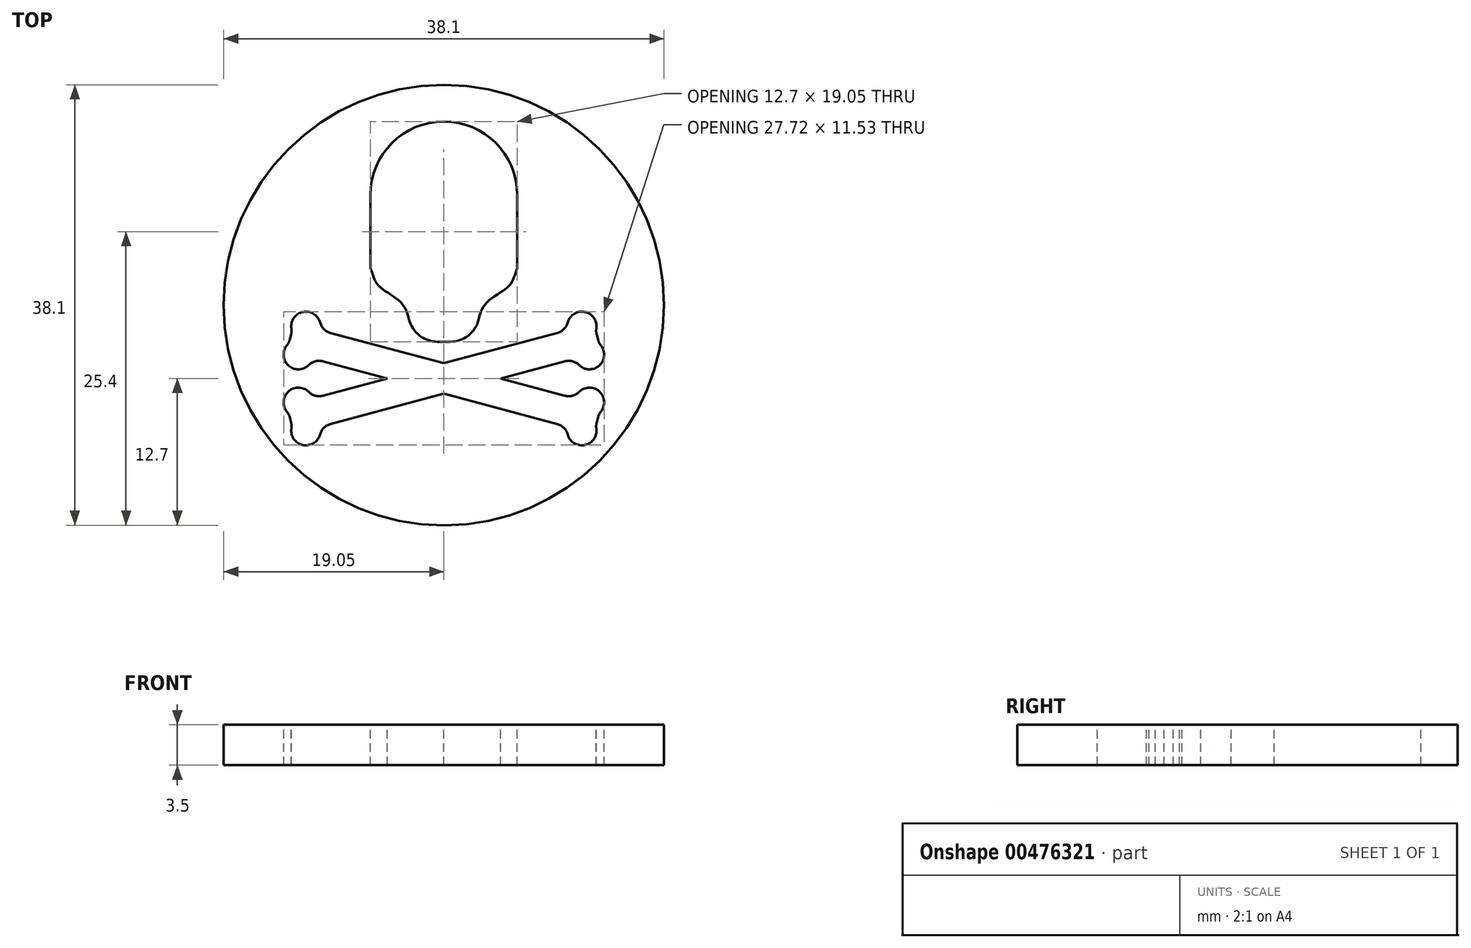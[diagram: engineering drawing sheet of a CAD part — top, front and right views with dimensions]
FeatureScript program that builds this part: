
annotation { "Feature Type Name" : "Feature", "Feature Type Description" : "" }
export const myFeature = defineFeature(function(context is Context, id is Id, definition is map)
    precondition{}
    {
        {
            var Q0;
            Q0=qCreatedBy(makeId("Top.planeOp"),FACE);
            var sketch = newSketch(context, id + "F0", { "sketchPlane" : qUnion([Q0])});
            skCircle(sketch, "E0", {"center": v(0, 0) * mm, "radius": 19.05 * mm});
            skSolve(sketch);
        }
        {
            var Q0;
            Q0=qSketchRegion(id+"F0",true);
            extrude(context, id + "F1", {"entities" : qUnion([Q0]), "depth" : 3.5 * mm});
        }
        {
            var Q0;
            Q0=makeQuery(id+"F1.opExtrude","CAP_FACE",FACE,{"disambiguationData":[OSD([sQuery(id+"F0.wireOp",EDGE,"E0")])],"isStart":false});
            var sketch = newSketch(context, id + "F2", { "sketchPlane" : qUnion([Q0])});
            skLineSegment(sketch, "E1.bottom", {"start": v(0, 15.88) * mm, "end": v(0, 15.88) * mm});
            skLineSegment(sketch, "E1.top", {"start": v(0.54, -3.18) * mm, "end": v(-0.54, -3.18) * mm});
            skLineSegment(sketch, "E1.left", {"start": v(6.35, 9.52) * mm, "end": v(6.35, 3.18) * mm});
            skLineSegment(sketch, "E1.right", {"start": v(-6.35, 9.52) * mm, "end": v(-6.35, 3.17) * mm});
            skPoint(sketch, "E1.middle", {"position": v(0, 6.35) * mm});
            skPoint(sketch, "E2.visualSharp", {"position": v(-6.35, 15.88) * mm});
            skArc(sketch, "E2.filletArc", {"start": v(0, 15.88) * mm, "mid": v(-4.5, 14.02) * mm, "end": v(-6.35, 9.52) * mm});
            skPoint(sketch, "E3.visualSharp", {"position": v(6.35, 15.88) * mm});
            skArc(sketch, "E3.filletArc", {"start": v(6.35, 9.52) * mm, "mid": v(4.5, 14.02) * mm, "end": v(0, 15.88) * mm});
            skFitSpline(sketch, "E4", {"points": [v(-6.35, 3.17) * mm, v(-5.66, 1.69) * mm, v(-3.53, 0) * mm, v(-2.54, -3.18) * mm], "startDerivative": vector(2.39, -5.8) * mm, "endDerivative": vector(3.14, -8.85) * mm});
            skLineSegment(sketch, "E5", {"start": v(0, 15.88) * mm, "end": v(0, -3.18) * mm});
            skFitSpline(sketch, "E6.MirrorCS", {"points": [v(6.35, 3.17) * mm, v(5.66, 1.69) * mm, v(3.53, 0) * mm, v(2.54, -3.17) * mm], "startDerivative": vector(-2.39, -5.8) * mm, "endDerivative": vector(-3.14, -8.85) * mm});
            skPoint(sketch, "E7.orphan", {"position": v(-6.35, -3.17) * mm});
            skPoint(sketch, "E8.orphan", {"position": v(6.35, -3.18) * mm});
            skArc(sketch, "E9.filletArc", {"start": v(-3.01, -1.24) * mm, "mid": v(-2.11, -2.63) * mm, "end": v(-0.54, -3.17) * mm});
            skPoint(sketch, "E10.visualSharp", {"position": v(2.54, -3.18) * mm});
            skArc(sketch, "E10.filletArc", {"start": v(0.54, -3.17) * mm, "mid": v(2.11, -2.63) * mm, "end": v(3.01, -1.24) * mm});
            skSolve(sketch);
        }
        {
            var Q0;
            Q0=qSketchRegion(id+"F2",true);
            extrude(context, id + "F3", {"entities" : qUnion([Q0]), "operationType" : NewBodyOperationType.REMOVE, "oppositeDirection" : true, "depth" : 5.33 * mm});
        }
        {
            var Q0;
            Q0=makeQuery(id+"F1.opExtrude","CAP_FACE",FACE,{"disambiguationData":[OSD([sQuery(id+"F0.wireOp",EDGE,"E0")])],"isStart":false});
            var sketch = newSketch(context, id + "F4", { "sketchPlane" : qUnion([Q0])});
            skLineSegment(sketch, "E11", {"start": v(-11.94, -1.84) * mm, "end": v(12.6, -8.41) * mm});
            skLineSegment(sketch, "E12", {"start": v(12.6, -8.41) * mm, "end": v(11.94, -10.86) * mm});
            skLineSegment(sketch, "E13", {"start": v(11.94, -10.86) * mm, "end": v(-12.6, -4.29) * mm});
            skLineSegment(sketch, "E14", {"start": v(-12.6, -4.29) * mm, "end": v(-11.94, -1.84) * mm});
            skLineSegment(sketch, "E15", {"start": v(-12.27, -3.06) * mm, "end": v(12.27, -9.64) * mm});
            skPoint(sketch, "E16", {"position": v(0, -6.35) * mm});
            skLineSegment(sketch, "E17", {"start": v(-12.6, -8.41) * mm, "end": v(9.81, -2.4) * mm});
            skLineSegment(sketch, "E18", {"start": v(11.94, -1.84) * mm, "end": v(12.6, -4.29) * mm});
            skLineSegment(sketch, "E19", {"start": v(10.47, -4.86) * mm, "end": v(-11.94, -10.86) * mm});
            skLineSegment(sketch, "E20", {"start": v(-11.94, -10.86) * mm, "end": v(-12.6, -8.41) * mm});
            skLineSegment(sketch, "E21", {"start": v(-12.27, -9.64) * mm, "end": v(12.27, -3.06) * mm});
            skLineSegment(sketch, "E22", {"start": v(0, 0) * mm, "end": v(0, -6.35) * mm});
            skArc(sketch, "E23", {"start": v(13.2, -2.03) * mm, "mid": v(12.2, -0.6) * mm, "end": v(10.71, -1.5) * mm});
            skArc(sketch, "E24", {"start": v(11.7, -5.19) * mm, "mid": v(13.44, -5.24) * mm, "end": v(13.59, -3.5) * mm});
            skLineSegment(sketch, "E25", {"start": v(13.22, -2.55) * mm, "end": v(13.35, -3.03) * mm});
            skPoint(sketch, "E26.visualSharp", {"position": v(13.14, -2.24) * mm});
            skArc(sketch, "E26.filletArc", {"start": v(13.2, -2.03) * mm, "mid": v(13.18, -2.3) * mm, "end": v(13.22, -2.55) * mm});
            skPoint(sketch, "E27.visualSharp", {"position": v(13.43, -3.33) * mm});
            skArc(sketch, "E27.filletArc", {"start": v(13.35, -3.03) * mm, "mid": v(13.45, -3.28) * mm, "end": v(13.59, -3.5) * mm});
            skPoint(sketch, "E28.visualSharp", {"position": v(10.71, -2.16) * mm});
            skArc(sketch, "E28.filletArc", {"start": v(9.81, -2.4) * mm, "mid": v(10.38, -2.08) * mm, "end": v(10.71, -1.5) * mm});
            skPoint(sketch, "E29.visualSharp", {"position": v(11.37, -4.62) * mm});
            skArc(sketch, "E29.filletArc", {"start": v(11.7, -5.19) * mm, "mid": v(11.13, -4.86) * mm, "end": v(10.47, -4.86) * mm});
            skLineSegment(sketch, "E30", {"start": v(0, -6.35) * mm, "end": v(13.76, -6.35) * mm});
            skArc(sketch, "E31.MirrorCS", {"start": v(11.7, -7.51) * mm, "mid": v(11.13, -7.84) * mm, "end": v(10.47, -7.84) * mm});
            skArc(sketch, "E32.MirrorCS", {"start": v(11.7, -7.51) * mm, "mid": v(13.44, -7.46) * mm, "end": v(13.59, -9.2) * mm});
            skArc(sketch, "E33.MirrorCS", {"start": v(13.35, -9.67) * mm, "mid": v(13.45, -9.42) * mm, "end": v(13.59, -9.2) * mm});
            skLineSegment(sketch, "E34.MirrorCS", {"start": v(13.22, -10.15) * mm, "end": v(13.35, -9.67) * mm});
            skArc(sketch, "E35.MirrorCS", {"start": v(13.2, -10.67) * mm, "mid": v(13.18, -10.4) * mm, "end": v(13.22, -10.15) * mm});
            skArc(sketch, "E36.MirrorCS", {"start": v(13.2, -10.67) * mm, "mid": v(12.2, -12.1) * mm, "end": v(10.71, -11.2) * mm});
            skArc(sketch, "E37.MirrorCS", {"start": v(9.81, -10.3) * mm, "mid": v(10.38, -10.62) * mm, "end": v(10.71, -11.2) * mm});
            skArc(sketch, "E38.MirrorCS", {"start": v(-13.2, -2.03) * mm, "mid": v(-12.2, -0.6) * mm, "end": v(-10.71, -1.5) * mm});
            skArc(sketch, "E39.MirrorCS", {"start": v(-9.81, -2.4) * mm, "mid": v(-10.38, -2.08) * mm, "end": v(-10.71, -1.5) * mm});
            skArc(sketch, "E40.MirrorCS", {"start": v(-11.7, -5.19) * mm, "mid": v(-13.44, -5.24) * mm, "end": v(-13.59, -3.5) * mm});
            skArc(sketch, "E41.MirrorCS", {"start": v(-11.7, -5.19) * mm, "mid": v(-11.13, -4.86) * mm, "end": v(-10.47, -4.86) * mm});
            skArc(sketch, "E42.MirrorCS", {"start": v(-13.35, -3.03) * mm, "mid": v(-13.45, -3.28) * mm, "end": v(-13.59, -3.5) * mm});
            skLineSegment(sketch, "E43.MirrorCS", {"start": v(-13.22, -2.55) * mm, "end": v(-13.35, -3.03) * mm});
            skArc(sketch, "E44.MirrorCS", {"start": v(-13.2, -2.03) * mm, "mid": v(-13.18, -2.3) * mm, "end": v(-13.22, -2.55) * mm});
            skArc(sketch, "E45.MirrorCS", {"start": v(-11.7, -7.51) * mm, "mid": v(-11.13, -7.84) * mm, "end": v(-10.47, -7.84) * mm});
            skArc(sketch, "E46.MirrorCS", {"start": v(-11.7, -7.51) * mm, "mid": v(-13.44, -7.46) * mm, "end": v(-13.59, -9.2) * mm});
            skArc(sketch, "E47.MirrorCS", {"start": v(-13.35, -9.67) * mm, "mid": v(-13.45, -9.42) * mm, "end": v(-13.59, -9.2) * mm});
            skLineSegment(sketch, "E48.MirrorCS", {"start": v(-13.22, -10.15) * mm, "end": v(-13.35, -9.67) * mm});
            skArc(sketch, "E49.MirrorCS", {"start": v(-13.2, -10.67) * mm, "mid": v(-13.18, -10.4) * mm, "end": v(-13.22, -10.15) * mm});
            skArc(sketch, "E50.MirrorCS", {"start": v(-13.2, -10.67) * mm, "mid": v(-12.2, -12.1) * mm, "end": v(-10.71, -11.2) * mm});
            skArc(sketch, "E51.MirrorCS", {"start": v(-9.81, -10.3) * mm, "mid": v(-10.38, -10.62) * mm, "end": v(-10.71, -11.2) * mm});
            skSolve(sketch);
        }
        {
            var Q0;
            Q0=qSketchRegion(id+"F4",true);
            var Q1;
            {var subQ0=sQuery(id+"F4.wireOp",EDGE,"79daabfb-e708-4f8d-b930-0284830156720.MirrorCS");Q1=makeQuery(id+"F4.imprint","IMPRINT",FACE,{"disambiguationData":[TD([[makeQuery(id+"F4.imprint","IMPRINT",EDGE,{"derivedFrom":subQ0}),-1.0]])]});}
            var Q2;
            {var subQ0=sQuery(id+"F4.wireOp",EDGE,"81815b4a-eb9a-46ba-bb84-2da79c74dedf0.MirrorCS");Q2=makeQuery(id+"F4.imprint","IMPRINT",FACE,{"disambiguationData":[TD([[makeQuery(id+"F4.imprint","IMPRINT",EDGE,{"derivedFrom":subQ0}),-1.0]])]});}
            var Q3;
            {var subQ0=sQuery(id+"F4.wireOp",EDGE,"f94ec01d-3a1b-4ee6-b849-c2fed6d013ab0.MirrorCS");var subQ1=sQuery(id+"F4.wireOp",EDGE,"nyevlk8L-7Z2X-lH10-pc4Y-s9fzSUyXAaBk");var subQ2=makeQuery(id+"F4.imprint","INTERSECT",VERTEX,{"derivedFrom":[subQ1,subQ0]});Q3=makeQuery(id+"F4.imprint","IMPRINT",FACE,{"disambiguationData":[TD([[makeQuery(id+"F4.imprint","IMPRINT",EDGE,{"disambiguationData":[TD([[subQ2,1.0]])],"derivedFrom":subQ1}),-1.0]])]});}
            var Q4;
            {var subQ0=sQuery(id+"F4.wireOp",EDGE,"6840b8d1-15e5-4749-b6c6-1a15b524e8780.MirrorCS");var subQ1=sQuery(id+"F4.wireOp",EDGE,"PieO4w4A-Decb-AyKF-tgIh-CT2OS44ABLdv");var subQ2=makeQuery(id+"F4.imprint","INTERSECT",VERTEX,{"derivedFrom":[subQ1,subQ0]});Q4=makeQuery(id+"F4.imprint","IMPRINT",FACE,{"disambiguationData":[TD([[makeQuery(id+"F4.imprint","IMPRINT",EDGE,{"disambiguationData":[TD([[subQ2,1.0]])],"derivedFrom":subQ1}),-1.0]])]});}
            extrude(context, id + "F5", {"entities" : qUnion([Q0, Q1, Q2, Q3, Q4]), "operationType" : NewBodyOperationType.REMOVE, "oppositeDirection" : true, "depth" : 25.4 * mm});
        }
    });
